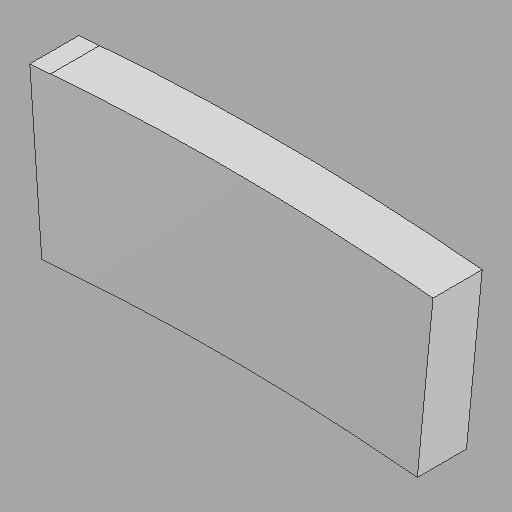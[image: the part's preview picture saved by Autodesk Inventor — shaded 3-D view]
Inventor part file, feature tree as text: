
AUTODESK INVENTOR PART (.ipt)
format: ipt  version: 2022.1 (Build 261234020, 234B)  size: 91,136 bytes
history: imported  units: in
note: dims shown in document units (in); Inventor stores cm internally (conversion verified against a paired STEP export)
features: imported_body x1
ambient origin geometry x8: Origin, YZ Plane, XZ Plane, XY Plane, X Axis, Y Axis, Z Axis, Center Point
bodies: Solid1 (imported_parasolid)
feature tree (1):
  imported_body  NMx_Import_Brep_tag  [imported B-rep: ~8 faces, bbox_mm=[1249.421707, 514.369354, 152.4]]
